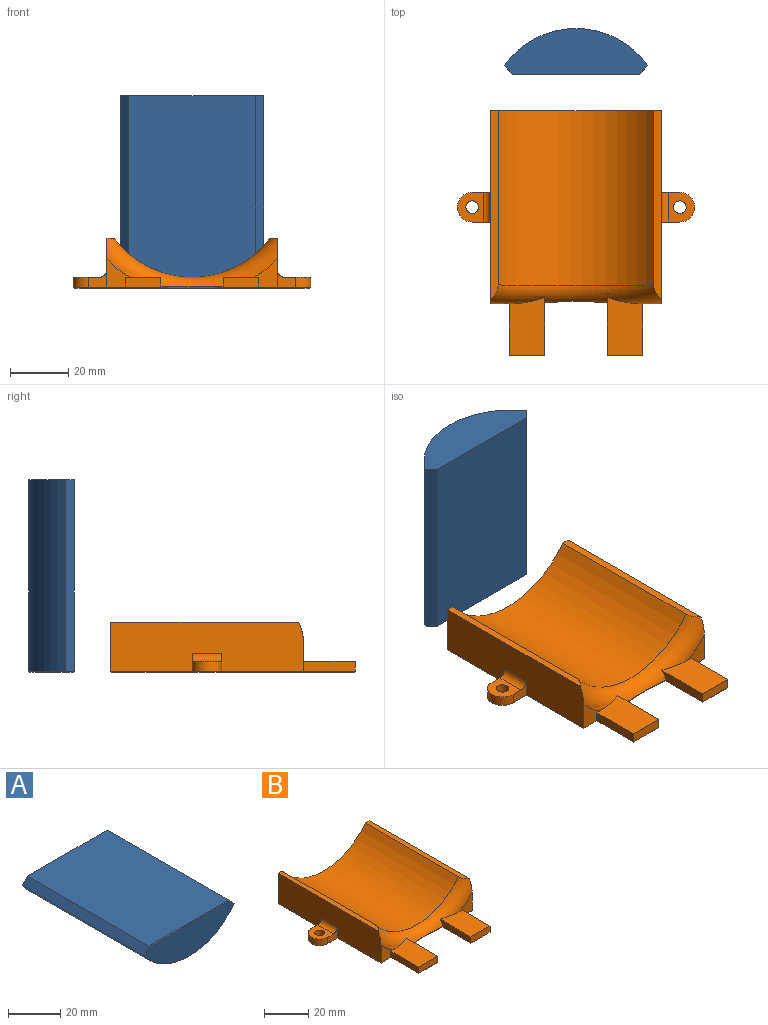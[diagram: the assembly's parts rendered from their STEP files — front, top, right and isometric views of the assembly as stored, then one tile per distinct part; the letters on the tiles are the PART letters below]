
ASSEMBLY  parts=2 mates=1
PART A: 10 faces, bbox 49.2x66x15.7 mm
  f0: plane 65.66x3.01mm, normal (-0.71,0,0.71), area 279.1mm2, adj f1,f3,f4,f9
  f1: cylinder r=30.23mm len=65.66mm, axis (0,-1,0), area 3772.9mm2, adj f0,f2,f4,f8
  f2: plane 65.66x3.01mm, normal (0.71,0,0.71), area 279.1mm2, adj f1,f3,f4,f6
  f3: plane 65.66x43.18mm, normal (0,0,1), area 2835.2mm2, adj f0,f2,f4,f7
  f4: plane 49.19x15.66mm, normal (0,1,0), area 575.2mm2, adj f0,f1,f2,f3
  f5: plane 48.19x14.9mm, normal (0,-1,0), area 534.1mm2, adj f6,f7,f8,f9
  f6: plane 3.17x3.05mm, normal (0.5,-0.71,0.5), area 2.2mm2, adj f2,f5,f7,f8
  f7: plane 43.18x0.38mm, normal (0,-0.71,0.71), area 23.2mm2, adj f3,f5,f6,f9
  f8: cone r=29.84mm half-angle=45deg, axis (0,1,0), area 30.6mm2, adj f1,f5,f6,f9
  f9: plane 3.17x3.05mm, normal (-0.5,-0.71,0.5), area 2.2mm2, adj f0,f5,f7,f8
PART B: 52 faces, bbox 81.9x84.4x29.7 mm
  f0: plane 9.88x7.7mm, normal (0,-1,0), area 44.3mm2, adj f1,f8,f13,f17,f40
  f1: plane 20.41x12.76mm, normal (0,0,1), area 224.7mm2, adj f0,f2,f13,f16,f17
  f2: plane 12.19x3.38mm, normal (0,-1,0), area 41.3mm2, adj f1,f13,f16,f36
  f3: plane 9.88x7.7mm, normal (0,-1,0), area 44.3mm2, adj f6,f11,f12,f17,f35
  f4: cylinder r=33.27mm len=59.69mm, axis (0,-1,0), area 3693.6mm2, adj f5,f9,f10,f17
  f5: plane 65.01x3.17mm, normal (0,0,1), area 159.8mm2, adj f4,f6,f10,f17
  f6: plane 66.22x16.94mm, normal (-1,0,0), area 1042.5mm2, adj f3,f5,f10,f17,f18,f21,f29,f37
  f7: plane 83.06x80.52mm, normal (0,0,-1), area 4313.8mm2, adj f30,f31,f32,f33,f34,f35,f36,f37
  f8: plane 66.19x16.91mm, normal (1,0,0), area 1042.5mm2, adj f0,f9,f10,f17,f23,f24,f28,f42
  f9: plane 65.01x3.17mm, normal (0,0,1), area 159.8mm2, adj f4,f8,f10,f17
  f10: plane 58.42x16.76mm, normal (0,1,0), area 480.3mm2, adj f4,f5,f6,f8,f9,f47
  f11: plane 20.41x12.76mm, normal (0,0,1), area 224.7mm2, adj f3,f12,f14,f15,f17
  f12: plane 17.78x3.38mm, normal (-1,0,0), area 60.2mm2, adj f3,f11,f14,f33
  f13: plane 17.78x3.38mm, normal (1,0,0), area 60.2mm2, adj f0,f1,f2,f38
  f14: plane 12.19x3.38mm, normal (0,-1,0), area 41.3mm2, adj f11,f12,f15,f31
  f15: plane 19.88x3.43mm, normal (1,0,0), area 63.2mm2, adj f11,f14,f17,f30,f32
  f16: plane 19.88x3.42mm, normal (-1,0,0), area 63.2mm2, adj f1,f2,f17,f32,f34
  f17: torus R=39.62mm, axis (0,-1,0), area 538.8mm2, adj f0,f1,f3,f4,f5,f6,f8,f9
  f18: plane 6.35x5.97mm, normal (0,-1,0), area 23.2mm2, adj f6,f19,f22,f29,f39
  f19: cylinder r=5.08mm len=10.16mm, axis (0,0,-1), area 54.7mm2, adj f18,f21,f22,f41
  f20: cylinder r=2.16mm len=4.32mm, axis (0,0,-1), area 46.5mm2, adj f22,f51
  f21: plane 6.35x5.97mm, normal (0,1,0), area 23.2mm2, adj f6,f19,f22,f29,f43
  f22: plane 10.16x8.89mm, normal (0,0,1), area 64.6mm2, adj f18,f19,f20,f21,f29
  f23: plane 6.35x5.97mm, normal (0,-1,0), area 23.2mm2, adj f8,f25,f27,f28,f44
  f24: plane 6.35x5.97mm, normal (0,1,0), area 23.2mm2, adj f8,f25,f27,f28,f48
  f25: cylinder r=5.08mm len=10.16mm, axis (0,0,-1), area 54.7mm2, adj f23,f24,f27,f46
  f26: cylinder r=2.16mm len=4.32mm, axis (0,0,-1), area 46.5mm2, adj f27,f50
  f27: plane 10.16x8.89mm, normal (0,0,1), area 64.6mm2, adj f23,f24,f25,f26,f28
  f28: cylinder r=2.54mm len=10.16mm, axis (0,-1,0), area 40.5mm2, adj f8,f23,f24,f27
  f29: cylinder r=2.54mm len=10.16mm, axis (0,-1,0), area 40.5mm2, adj f6,f18,f21,f22
  f30: plane 18.32x0.38mm, normal (0.71,0,-0.71), area 9.7mm2, adj f7,f15,f31,f32
  f31: plane 12.19x0.38mm, normal (0,-0.71,-0.71), area 6.4mm2, adj f7,f14,f30,f33
  f32: bspline ~24.31x1.08mm, area 13.8mm2, adj f7,f15,f16,f17,f30,f34
  f33: plane 18.16x0.38mm, normal (-0.71,0,-0.71), area 9.6mm2, adj f7,f12,f31,f35
  f34: plane 18.32x0.38mm, normal (-0.71,0,-0.71), area 9.7mm2, adj f7,f16,f32,f36
  f35: plane 6.73x0.38mm, normal (0,-0.71,-0.71), area 3.4mm2, adj f3,f7,f33,f37
  f36: plane 12.19x0.38mm, normal (0,-0.71,-0.71), area 6.4mm2, adj f2,f7,f34,f38
  f37: plane 28.32x0.38mm, normal (-0.71,0,-0.71), area 15.1mm2, adj f6,f7,f35,f39
  f38: plane 18.16x0.38mm, normal (0.71,0,-0.71), area 9.6mm2, adj f7,f13,f36,f40
  f39: plane 6.73x0.38mm, normal (0,-0.71,-0.71), area 3.5mm2, adj f7,f18,f37,f41
  f40: plane 6.73x0.38mm, normal (0,-0.71,-0.71), area 3.4mm2, adj f0,f7,f38,f42
  f41: cone r=4.7mm half-angle=45deg, axis (0,0,1), area 8.3mm2, adj f7,f19,f39,f43
  f42: plane 28.32x0.38mm, normal (0.71,0,-0.71), area 15.1mm2, adj f7,f8,f40,f44
  f43: plane 6.73x0.38mm, normal (0,0.71,-0.71), area 3.5mm2, adj f7,f21,f41,f45
  f44: plane 6.73x0.38mm, normal (0,-0.71,-0.71), area 3.5mm2, adj f7,f23,f42,f46
  f45: plane 28.32x0.38mm, normal (-0.71,0,-0.71), area 15.1mm2, adj f6,f7,f43,f47
  f46: cone r=4.7mm half-angle=45deg, axis (0,0,1), area 8.3mm2, adj f7,f25,f44,f48
  f47: plane 58.42x0.38mm, normal (0,0.71,-0.71), area 31.3mm2, adj f7,f10,f45,f49
  f48: plane 6.73x0.38mm, normal (0,0.71,-0.71), area 3.5mm2, adj f7,f24,f46,f49
  f49: plane 28.32x0.38mm, normal (0.71,0,-0.71), area 15.1mm2, adj f7,f8,f47,f48
  f50: cone r=2.16mm half-angle=45deg, axis (0,0,-1), area 8mm2, adj f7,f26
  f51: cone r=2.16mm half-angle=45deg, axis (0,0,-1), area 8mm2, adj f7,f20
PLACE A rot(axis=(1,0,0),90deg) t=(0,-1.53,0)mm
PLACE B t=(0,-85.08,17.14)mm
MATE fastened B.f7 <-> A.f5  axis (0,0,-1) through (0,-55.88,0)mm
